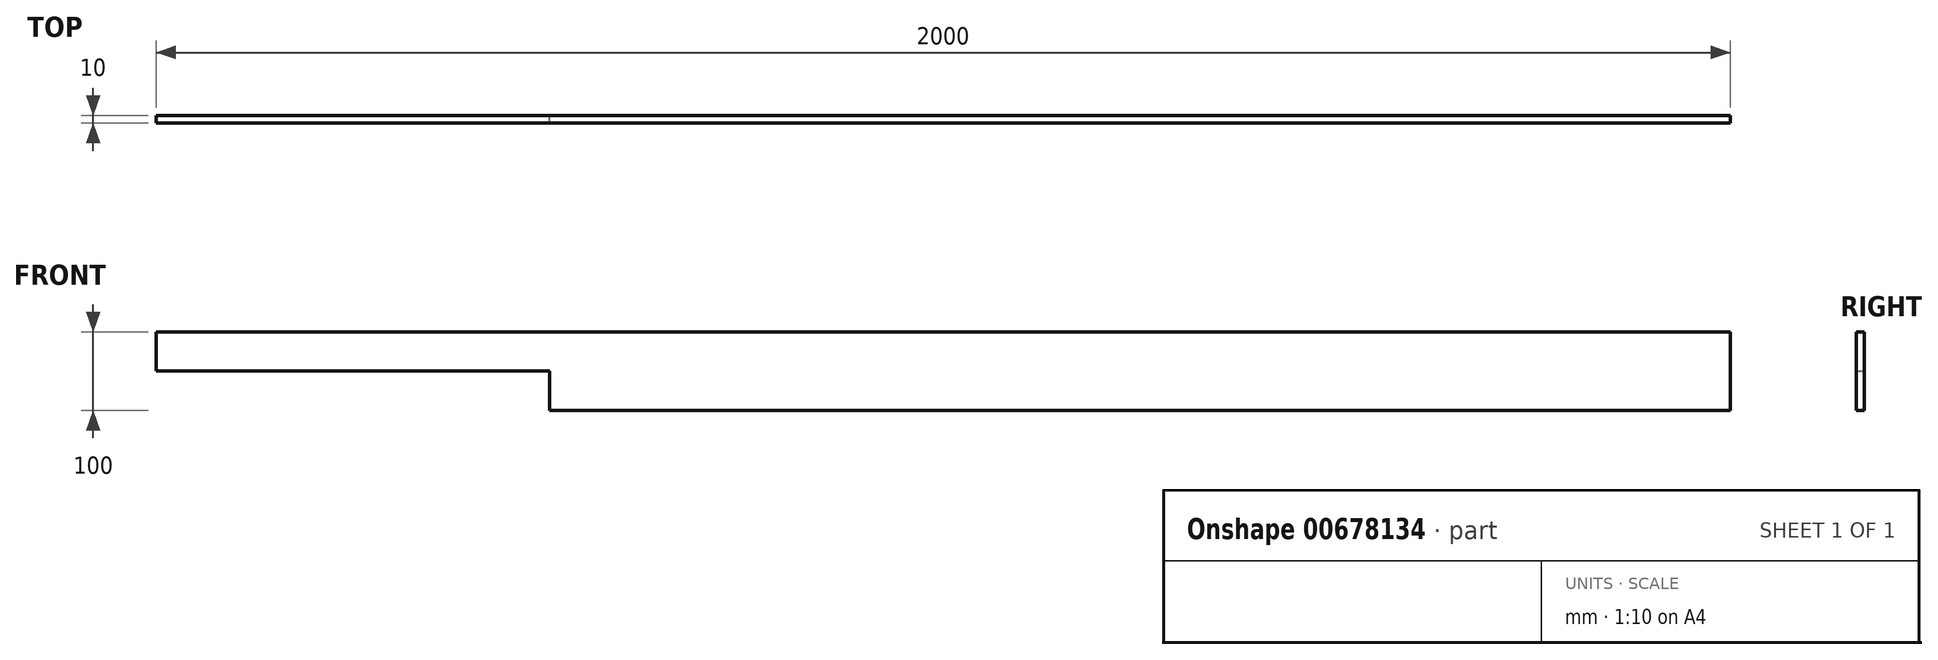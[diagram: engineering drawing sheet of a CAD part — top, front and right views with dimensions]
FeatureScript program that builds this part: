
annotation { "Feature Type Name" : "Feature", "Feature Type Description" : "" }
export const myFeature = defineFeature(function(context is Context, id is Id, definition is map)
    precondition{}
    {
        {
            var Q0;
            Q0=qCreatedBy(makeId("Front.planeOp"),FACE);
            var sketch = newSketch(context, id + "F0", { "sketchPlane" : qUnion([Q0])});
            skLineSegment(sketch, "E0.bottom", {"start": v(1000, 50) * mm, "end": v(-1000, 50) * mm});
            skLineSegment(sketch, "E0.top", {"start": v(1000, -50) * mm, "end": v(-500, -50) * mm});
            skLineSegment(sketch, "E0.left", {"start": v(1000, 50) * mm, "end": v(1000, -50) * mm});
            skLineSegment(sketch, "E0.right", {"start": v(-1000, 50) * mm, "end": v(-1000, 0) * mm});
            skPoint(sketch, "E0.middle", {"position": v(0, 0) * mm});
            skLineSegment(sketch, "E1.top", {"start": v(-1000, 0) * mm, "end": v(-500, 0) * mm});
            skLineSegment(sketch, "E1.right", {"start": v(-500, -50) * mm, "end": v(-500, 0) * mm});
            skPoint(sketch, "E2.orphan", {"position": v(-1000, -50) * mm});
            skSolve(sketch);
        }
        {
            var Q0;
            Q0=makeQuery(id+"F0.imprint","IMPRINT",FACE,{"disambiguationData":[TD([[makeQuery(id+"F0.imprint","IMPRINT",EDGE,{"derivedFrom":sQuery(id+"F0.wireOp",EDGE,"E0.bottom")}),1.0]])]});
            extrude(context, id + "F1", {"entities" : qUnion([Q0]), "depth" : 10 * mm, "offsetDistance" : 25 * mm});
        }
    });
